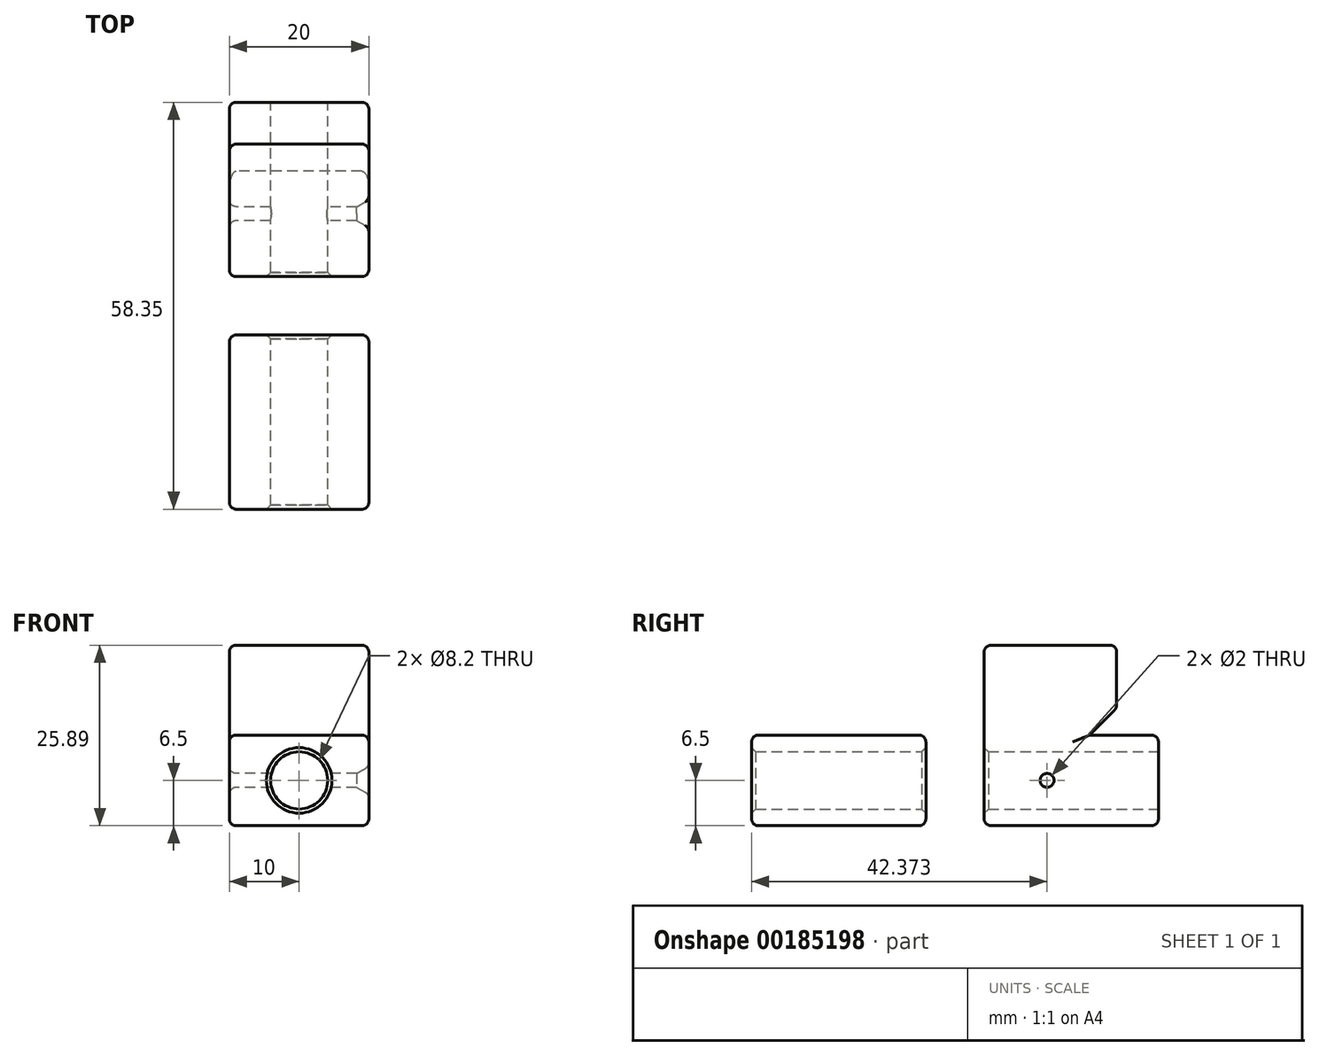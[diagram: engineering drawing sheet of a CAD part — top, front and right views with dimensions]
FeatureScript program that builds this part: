
annotation { "Feature Type Name" : "Feature", "Feature Type Description" : "" }
export const myFeature = defineFeature(function(context is Context, id is Id, definition is map)
    precondition{}
    {
        {
            var Q0;
            Q0=qCreatedBy(makeId("Right.planeOp"),FACE);
            var sketch = newSketch(context, id + "F0", { "sketchPlane" : qUnion([Q0])});
            skLineSegment(sketch, "E0", {"start": v(-13.48, 8.94) * mm, "end": v(-13.48, -16.95) * mm});
            skLineSegment(sketch, "E1", {"start": v(-13.48, -16.95) * mm, "end": v(11.52, -16.95) * mm});
            skLineSegment(sketch, "E2", {"start": v(11.52, -16.95) * mm, "end": v(11.52, -3.95) * mm});
            skLineSegment(sketch, "E3", {"start": v(11.52, -3.95) * mm, "end": v(1.63, -3.95) * mm});
            skLineSegment(sketch, "E4", {"start": v(1.63, -3.95) * mm, "end": v(5.52, -0.06) * mm});
            skLineSegment(sketch, "E5", {"start": v(5.52, -0.06) * mm, "end": v(5.52, 8.94) * mm});
            skLineSegment(sketch, "E6", {"start": v(5.52, 8.94) * mm, "end": v(-13.48, 8.94) * mm});
            skPoint(sketch, "E7.firstSnap0", {"position": v(6.57, -3.95) * mm});
            skLineSegment(sketch, "E7.bottom", {"start": v(-21.83, -3.95) * mm, "end": v(-46.83, -3.95) * mm});
            skLineSegment(sketch, "E7.top", {"start": v(-21.83, -16.95) * mm, "end": v(-46.83, -16.95) * mm});
            skLineSegment(sketch, "E7.left", {"start": v(-21.83, -3.95) * mm, "end": v(-21.83, -16.95) * mm});
            skLineSegment(sketch, "E7.right", {"start": v(-46.83, -3.95) * mm, "end": v(-46.83, -16.95) * mm});
            skLineSegment(sketch, "E8", {"start": v(11.52, -10.45) * mm, "end": v(-50.07, -10.45) * mm, "construction": true});
            skPoint(sketch, "E8.endSnap0", {"position": v(-46.83, -10.45) * mm});
            skSolve(sketch);
        }
        {
            var Q0;
            Q0=qSketchRegion(id+"F0",true);
            extrude(context, id + "F1", {"entities" : qUnion([Q0]), "depth" : 20 * mm});
        }
        {
            var Q0;
            Q0=makeQuery(id+"F1.opExtrude","SWEPT_FACE",FACE,{"disambiguationData":[OSD([sQuery(id+"F0.wireOp",EDGE,"E2")])]});
            var sketch = newSketch(context, id + "F2", { "sketchPlane" : qUnion([Q0])});
            skCircle(sketch, "E9", {"center": v(-10, -10.45) * mm, "radius": 4.1 * mm});
            skLineSegment(sketch, "E10", {"start": v(0, -10.45) * mm, "end": v(-20, -10.45) * mm, "construction": true});
            skSolve(sketch);
        }
        {
            var Q0;
            Q0=qSketchRegion(id+"F2",true);
            extrude(context, id + "F3", {"entities" : qUnion([Q0]), "operationType" : NewBodyOperationType.REMOVE, "endBound" : BoundingType.THROUGH_ALL, "oppositeDirection" : true, "depth" : 25 * mm});
        }
        {
            var Q0;
            Q0=makeQuery(id+"F1.opExtrude","CAP_FACE",FACE,{"disambiguationData":[OSD([sQuery(id+"F0.wireOp",EDGE,"E0"),sQuery(id+"F0.wireOp",EDGE,"E1"),sQuery(id+"F0.wireOp",EDGE,"E2"),sQuery(id+"F0.wireOp",EDGE,"E3"),sQuery(id+"F0.wireOp",EDGE,"E4"),sQuery(id+"F0.wireOp",EDGE,"E5"),sQuery(id+"F0.wireOp",EDGE,"E6")])],"isStart":true});
            var sketch = newSketch(context, id + "F4", { "sketchPlane" : qUnion([Q0])});
            skCircle(sketch, "E11", {"center": v(4.46, -10.45) * mm, "radius": 1 * mm});
            skSolve(sketch);
        }
        {
            var Q0;
            Q0=qSketchRegion(id+"F4",true);
            extrude(context, id + "F5", {"entities" : qUnion([Q0]), "operationType" : NewBodyOperationType.REMOVE, "endBound" : BoundingType.THROUGH_ALL, "oppositeDirection" : true, "depth" : 25 * mm});
        }
        {
            var Q0;
            Q0=makeQuery(id+"F5.boolean.opBoolean","COPY",EDGE,{"derivedFrom":makeQuery(id+"F5.opExtrude","CAP_EDGE",EDGE,{"disambiguationData":[OSD([sQuery(id+"F4.wireOp",EDGE,"E11")])],"isStart":true})});
            var Q1;
            Q1=makeQuery(id+"F5.boolean.opBoolean","INTERSECT",EDGE,{"derivedFrom":[makeQuery(id+"F1.opExtrude","CAP_FACE",FACE,{"disambiguationData":[OSD([sQuery(id+"F0.wireOp",EDGE,"E0"),sQuery(id+"F0.wireOp",EDGE,"E1"),sQuery(id+"F0.wireOp",EDGE,"E2"),sQuery(id+"F0.wireOp",EDGE,"E3"),sQuery(id+"F0.wireOp",EDGE,"E4"),sQuery(id+"F0.wireOp",EDGE,"E5"),sQuery(id+"F0.wireOp",EDGE,"E6")])],"isStart":false}),makeQuery(id+"F5.opExtrude","SWEPT_FACE",FACE,{"disambiguationData":[OSD([sQuery(id+"F4.wireOp",EDGE,"E11")])]})]});
            chamfer(context, id + "F6", {"entities" : qUnion([Q0, Q1]), "chamferType" : ChamferType.OFFSET_ANGLE, "width" : 1 * mm, "oppositeDirection" : false, "angle" : 60 * degree, "tangentPropagation" : true});
        }
        {
            var Q0;
            Q0=makeQuery(id+"F1.opExtrude","SWEPT_FACE",FACE,{"disambiguationData":[OSD([sQuery(id+"F0.wireOp",EDGE,"E6")])]});
            var Q1;
            Q1=makeQuery(id+"F1.opExtrude","CAP_FACE",FACE,{"disambiguationData":[OSD([sQuery(id+"F0.wireOp",EDGE,"E0"),sQuery(id+"F0.wireOp",EDGE,"E1"),sQuery(id+"F0.wireOp",EDGE,"E2"),sQuery(id+"F0.wireOp",EDGE,"E3"),sQuery(id+"F0.wireOp",EDGE,"E4"),sQuery(id+"F0.wireOp",EDGE,"E5"),sQuery(id+"F0.wireOp",EDGE,"E6")])],"isStart":true});
            var Q2;
            Q2=makeQuery(id+"F1.opExtrude","CAP_FACE",FACE,{"disambiguationData":[OSD([sQuery(id+"F0.wireOp",EDGE,"E0"),sQuery(id+"F0.wireOp",EDGE,"E1"),sQuery(id+"F0.wireOp",EDGE,"E2"),sQuery(id+"F0.wireOp",EDGE,"E3"),sQuery(id+"F0.wireOp",EDGE,"E4"),sQuery(id+"F0.wireOp",EDGE,"E5"),sQuery(id+"F0.wireOp",EDGE,"E6")])],"isStart":false});
            var Q3;
            Q3=makeQuery(id+"F1.opExtrude","SWEPT_FACE",FACE,{"disambiguationData":[OSD([sQuery(id+"F0.wireOp",EDGE,"E1")])]});
            var Q4;
            Q4=makeQuery(id+"F1.opExtrude","SWEPT_EDGE",EDGE,{"disambiguationData":[OSD([sQuery(id+"F0.wireOp",EDGE,"E2"),sQuery(id+"F0.wireOp",EDGE,"E3")])]});
            var Q5;
            Q5=makeQuery(id+"F1.opExtrude","SWEPT_EDGE",EDGE,{"disambiguationData":[OSD([sQuery(id+"F0.wireOp",EDGE,"E4"),sQuery(id+"F0.wireOp",EDGE,"E5")])]});
            var Q6;
            Q6=makeQuery(id+"F1.opExtrude","SWEPT_FACE",FACE,{"disambiguationData":[OSD([sQuery(id+"F0.wireOp",EDGE,"E7.bottom")])]});
            var Q7;
            Q7=makeQuery(id+"F1.opExtrude","CAP_FACE",FACE,{"disambiguationData":[OSD([sQuery(id+"F0.wireOp",EDGE,"E7.bottom"),sQuery(id+"F0.wireOp",EDGE,"E7.top"),sQuery(id+"F0.wireOp",EDGE,"E7.left"),sQuery(id+"F0.wireOp",EDGE,"E7.right")])],"isStart":true});
            var Q8;
            Q8=makeQuery(id+"F1.opExtrude","SWEPT_FACE",FACE,{"disambiguationData":[OSD([sQuery(id+"F0.wireOp",EDGE,"E7.top")])]});
            var Q9;
            Q9=makeQuery(id+"F1.opExtrude","CAP_FACE",FACE,{"disambiguationData":[OSD([sQuery(id+"F0.wireOp",EDGE,"E7.bottom"),sQuery(id+"F0.wireOp",EDGE,"E7.top"),sQuery(id+"F0.wireOp",EDGE,"E7.left"),sQuery(id+"F0.wireOp",EDGE,"E7.right")])],"isStart":false});
            fillet(context, id + "F7", {"entities" : qUnion([Q0, Q1, Q2, Q3, Q4, Q5, Q6, Q7, Q8, Q9]), "radius" : 1 * mm, "tangentPropagation" : true, "allowEdgeOverflow" : false});
        }
        {
            var Q0;
            Q0=makeQuery(id+"F3.boolean.opBoolean","COPY",EDGE,{"derivedFrom":makeQuery(id+"F3.opExtrude","CAP_EDGE",EDGE,{"disambiguationData":[OSD([sQuery(id+"F2.wireOp",EDGE,"E9")])],"isStart":true})});
            var Q1;
            Q1=makeQuery(id+"F3.boolean.opBoolean","INTERSECT",EDGE,{"derivedFrom":[makeQuery(id+"F1.opExtrude","SWEPT_FACE",FACE,{"disambiguationData":[OSD([sQuery(id+"F0.wireOp",EDGE,"E0")])]}),makeQuery(id+"F3.opExtrude","SWEPT_FACE",FACE,{"disambiguationData":[OSD([sQuery(id+"F2.wireOp",EDGE,"E9")])]})]});
            var Q2;
            Q2=makeQuery(id+"F3.boolean.opBoolean","INTERSECT",EDGE,{"derivedFrom":[makeQuery(id+"F1.opExtrude","SWEPT_FACE",FACE,{"disambiguationData":[OSD([sQuery(id+"F0.wireOp",EDGE,"E7.right")])]}),makeQuery(id+"F3.opExtrude","SWEPT_FACE",FACE,{"disambiguationData":[OSD([sQuery(id+"F2.wireOp",EDGE,"E9")])]})]});
            var Q3;
            Q3=makeQuery(id+"F3.boolean.opBoolean","INTERSECT",EDGE,{"derivedFrom":[makeQuery(id+"F1.opExtrude","SWEPT_FACE",FACE,{"disambiguationData":[OSD([sQuery(id+"F0.wireOp",EDGE,"E7.left")])]}),makeQuery(id+"F3.opExtrude","SWEPT_FACE",FACE,{"disambiguationData":[OSD([sQuery(id+"F2.wireOp",EDGE,"E9")])]})]});
            chamfer(context, id + "F8", {"entities" : qUnion([Q0, Q1, Q2, Q3]), "width" : 0.6 * mm, "tangentPropagation" : true});
        }
    });
